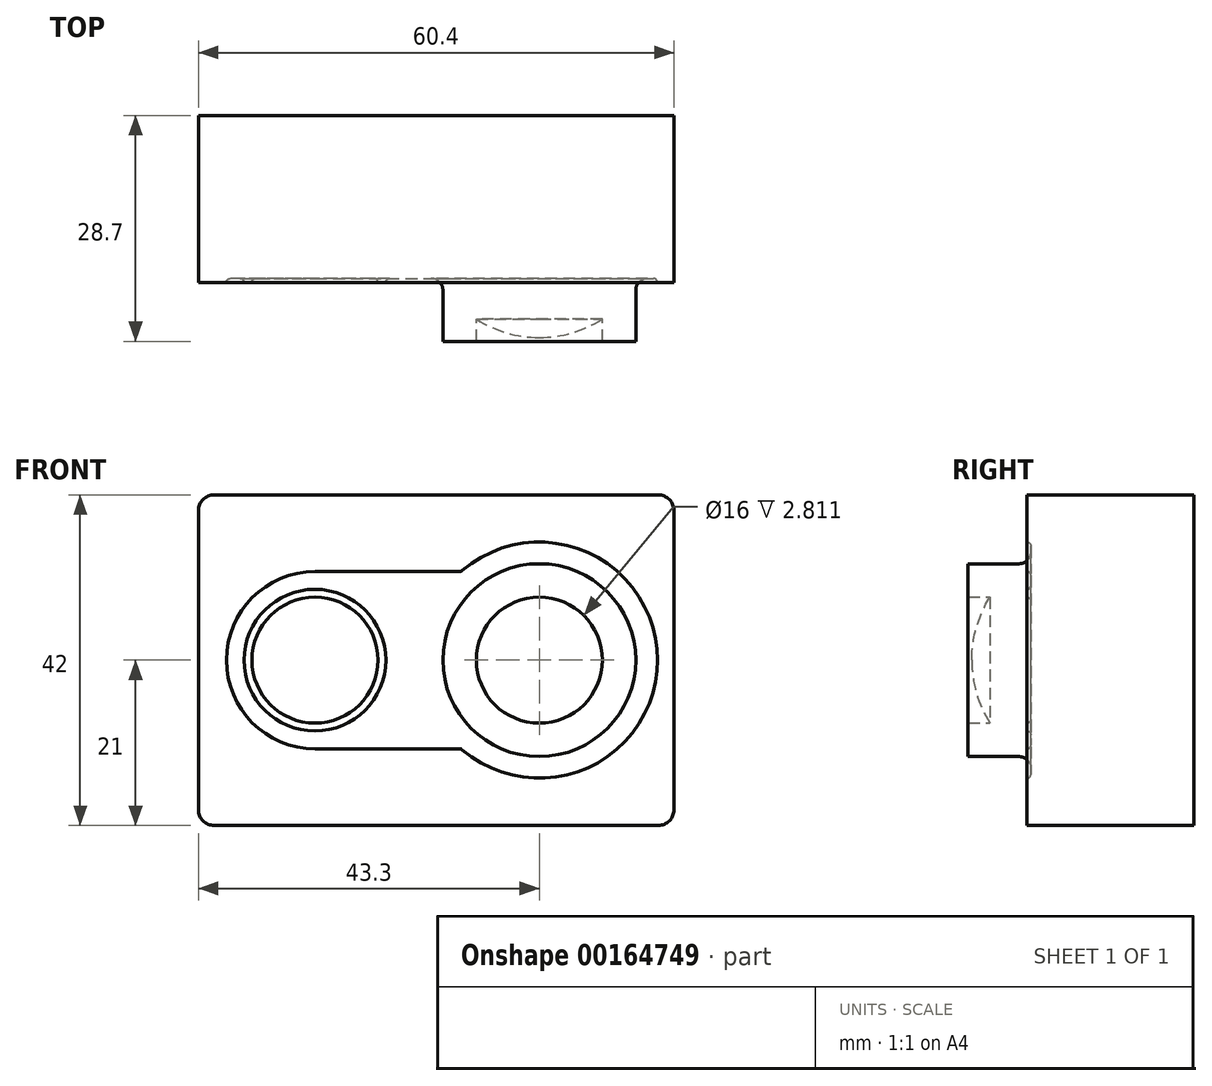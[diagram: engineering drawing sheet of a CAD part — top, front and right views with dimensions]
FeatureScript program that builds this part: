
annotation { "Feature Type Name" : "Feature", "Feature Type Description" : "" }
export const myFeature = defineFeature(function(context is Context, id is Id, definition is map)
    precondition{}
    {
        {
            var Q0;
            Q0=qCreatedBy(makeId("Front.planeOp"),FACE);
            var sketch = newSketch(context, id + "F0", { "sketchPlane" : qUnion([Q0])});
            skLineSegment(sketch, "E0.bottom", {"start": v(-30.2, 42) * mm, "end": v(30.2, 42) * mm});
            skLineSegment(sketch, "E0.top", {"start": v(-30.2, 0) * mm, "end": v(30.2, 0) * mm});
            skLineSegment(sketch, "E0.left", {"start": v(-30.2, 42) * mm, "end": v(-30.2, 0) * mm});
            skLineSegment(sketch, "E0.right", {"start": v(30.2, 42) * mm, "end": v(30.2, 0) * mm});
            skSolve(sketch);
        }
        {
            var Q0;
            Q0=makeQuery(id+"F0.imprint","IMPRINT",FACE,{"disambiguationData":[TD([[makeQuery(id+"F0.imprint","IMPRINT",EDGE,{"derivedFrom":sQuery(id+"F0.wireOp",EDGE,"E0.bottom")}),-1.0]])]});
            extrude(context, id + "F1", {"entities" : qUnion([Q0]), "depth" : 21.2 * mm});
        }
        {
            var Q0;
            Q0=makeQuery(id+"F1.opExtrude","SWEPT_EDGE",EDGE,{"disambiguationData":[OSD([sQuery(id+"F0.wireOp",EDGE,"E0.bottom"),sQuery(id+"F0.wireOp",EDGE,"E0.left")])]});
            var Q1;
            Q1=makeQuery(id+"F1.opExtrude","SWEPT_EDGE",EDGE,{"disambiguationData":[OSD([sQuery(id+"F0.wireOp",EDGE,"E0.bottom"),sQuery(id+"F0.wireOp",EDGE,"E0.right")])]});
            var Q2;
            Q2=makeQuery(id+"F1.opExtrude","SWEPT_EDGE",EDGE,{"disambiguationData":[OSD([sQuery(id+"F0.wireOp",EDGE,"E0.top"),sQuery(id+"F0.wireOp",EDGE,"E0.right")])]});
            var Q3;
            Q3=makeQuery(id+"F1.opExtrude","SWEPT_EDGE",EDGE,{"disambiguationData":[OSD([sQuery(id+"F0.wireOp",EDGE,"E0.top"),sQuery(id+"F0.wireOp",EDGE,"E0.left")])]});
            fillet(context, id + "F2", {"entities" : qUnion([Q0, Q1, Q2, Q3]), "radius" : 2 * mm, "tangentPropagation" : true, "allowEdgeOverflow" : false});
        }
        {
            var Q0;
            Q0=makeQuery(id+"F1.opExtrude","CAP_FACE",FACE,{"disambiguationData":[OSD([sQuery(id+"F0.wireOp",EDGE,"E0.bottom"),sQuery(id+"F0.wireOp",EDGE,"E0.top"),sQuery(id+"F0.wireOp",EDGE,"E0.left"),sQuery(id+"F0.wireOp",EDGE,"E0.right")])],"isStart":false});
            var sketch = newSketch(context, id + "F3", { "sketchPlane" : qUnion([Q0])});
            skCircle(sketch, "E1", {"center": v(-15.4, 21) * mm, "radius": 9 * mm});
            skCircle(sketch, "E2", {"center": v(13.1, 21) * mm, "radius": 12.25 * mm});
            skCircle(sketch, "E3", {"center": v(-15.4, 21) * mm, "radius": 8 * mm});
            skArc(sketch, "E4", {"start": v(3.32, 9.63) * mm, "mid": v(28.1, 21) * mm, "end": v(3.32, 32.37) * mm});
            skArc(sketch, "E5", {"start": v(-15.4, 32.25) * mm, "mid": v(-26.65, 21) * mm, "end": v(-15.4, 9.75) * mm});
            skLineSegment(sketch, "E6", {"start": v(-15.4, 32.25) * mm, "end": v(3, 32.25) * mm});
            skLineSegment(sketch, "E7", {"start": v(-15.4, 9.75) * mm, "end": v(3, 9.75) * mm});
            skPoint(sketch, "E8.visualSharp", {"position": v(3.18, 32.25) * mm});
            skArc(sketch, "E8.filletArc", {"start": v(3, 32.25) * mm, "mid": v(3.17, 32.28) * mm, "end": v(3.32, 32.37) * mm});
            skPoint(sketch, "E9.visualSharp", {"position": v(3.18, 9.75) * mm});
            skArc(sketch, "E9.filletArc", {"start": v(3.32, 9.63) * mm, "mid": v(3.17, 9.72) * mm, "end": v(3, 9.75) * mm});
            skSolve(sketch);
        }
        {
            var Q0;
            Q0=makeQuery(id+"F3.imprint","IMPRINT",FACE,{"disambiguationData":[TD([[makeQuery(id+"F3.imprint","IMPRINT",EDGE,{"derivedFrom":sQuery(id+"F3.wireOp",EDGE,"E1")}),-1.0]])]});
            extrude(context, id + "F4", {"entities" : qUnion([Q0]), "operationType" : NewBodyOperationType.REMOVE, "oppositeDirection" : true, "depth" : 0.5 * mm});
        }
        {
            var Q0;
            Q0=makeQuery(id+"F3.imprint","IMPRINT",FACE,{"disambiguationData":[TD([[makeQuery(id+"F3.imprint","IMPRINT",EDGE,{"derivedFrom":sQuery(id+"F3.wireOp",EDGE,"E3")}),1.0]])]});
            extrude(context, id + "F5", {"entities" : qUnion([Q0]), "operationType" : NewBodyOperationType.REMOVE, "oppositeDirection" : true, "depth" : 0.5 * mm});
        }
        {
            var Q0;
            Q0=makeQuery(id+"F3.imprint","IMPRINT",FACE,{"disambiguationData":[TD([[makeQuery(id+"F3.imprint","IMPRINT",EDGE,{"derivedFrom":sQuery(id+"F3.wireOp",EDGE,"E2")}),1.0]])]});
            extrude(context, id + "F6", {"entities" : qUnion([Q0]), "operationType" : NewBodyOperationType.ADD, "depth" : 7.5 * mm});
        }
        {
            var Q0;
            Q0=qCreatedBy(makeId("Right.planeOp"),FACE);
            cPlane(context, id + "F7", {"entities" : qUnion([Q0]), "cplaneType" : CPlaneType.OFFSET, "offset" : 13.1 * mm, "width" : 150 * mm, "height" : 150 * mm});
        }
        {
            var Q0;
            Q0=qCreatedBy(id+"F7.planeOp",FACE);
            var sketch = newSketch(context, id + "F8", { "sketchPlane" : qUnion([Q0])});
            skLineSegment(sketch, "E10", {"start": v(-28.7, 21) * mm, "end": v(0, 21) * mm, "construction": true});
            skArc(sketch, "E11", {"start": v(-25.89, 29) * mm, "mid": v(-27.61, 25.16) * mm, "end": v(-28.2, 21) * mm});
            skLineSegment(sketch, "E12", {"start": v(-25.89, 29) * mm, "end": v(-28.7, 29) * mm});
            skLineSegment(sketch, "E13", {"start": v(-28.7, 29) * mm, "end": v(-28.7, 21) * mm});
            skLineSegment(sketch, "E14", {"start": v(-28.7, 21) * mm, "end": v(-28.2, 21) * mm});
            skSolve(sketch);
        }
        {
            var Q0;
            Q0=makeQuery(id+"F8.imprint","IMPRINT",FACE,{"disambiguationData":[TD([[makeQuery(id+"F8.imprint","IMPRINT",EDGE,{"derivedFrom":sQuery(id+"F8.wireOp",EDGE,"E11")}),-1.0]])]});
            var Q1;
            Q1=sQuery(id+"F8.wireOp",EDGE,"E10");
            revolve(context, id + "F9", {"operationType" : NewBodyOperationType.REMOVE, "entities" : qUnion([Q0]), "axis" : qUnion([Q1]), "revolveType" : RevolveType.FULL, "oppositeDirection" : true});
        }
        {
            var Q0;
            Q0=makeQuery(id+"F4.boolean.opBoolean","COPY",EDGE,{"derivedFrom":makeQuery(id+"F4.opExtrude","CAP_EDGE",EDGE,{"disambiguationData":[OSD([sQuery(id+"F3.wireOp",EDGE,"E2")])],"isStart":false})});
            fillet(context, id + "F10", {"entities" : qUnion([Q0]), "radius" : 1.5 * mm, "tangentPropagation" : true, "allowEdgeOverflow" : false});
        }
        {
            var Q0;
            Q0=makeQuery(id+"F4.boolean.opBoolean","COPY",FACE,{"derivedFrom":makeQuery(id+"F4.opExtrude","CAP_FACE",FACE,{"disambiguationData":[OSD([sQuery(id+"F3.wireOp",EDGE,"E1"),sQuery(id+"F3.wireOp",EDGE,"E2"),sQuery(id+"F3.wireOp",EDGE,"E4"),sQuery(id+"F3.wireOp",EDGE,"E5"),sQuery(id+"F3.wireOp",EDGE,"E6"),sQuery(id+"F3.wireOp",EDGE,"E7"),sQuery(id+"F3.wireOp",EDGE,"E8.filletArc"),sQuery(id+"F3.wireOp",EDGE,"E9.filletArc")])],"isStart":false})});
            fillet(context, id + "F11", {"entities" : qUnion([Q0]), "radius" : 0.5 * mm, "tangentPropagation" : true, "allowEdgeOverflow" : false});
        }
        {
            var Q0;
            Q0=makeQuery(id+"F5.boolean.opBoolean","COPY",FACE,{"derivedFrom":makeQuery(id+"F5.opExtrude","CAP_FACE",FACE,{"disambiguationData":[OSD([sQuery(id+"F3.wireOp",EDGE,"E3")])],"isStart":false})});
            fillet(context, id + "F12", {"entities" : qUnion([Q0]), "radius" : 0.5 * mm, "tangentPropagation" : true, "allowEdgeOverflow" : false});
        }
    });
